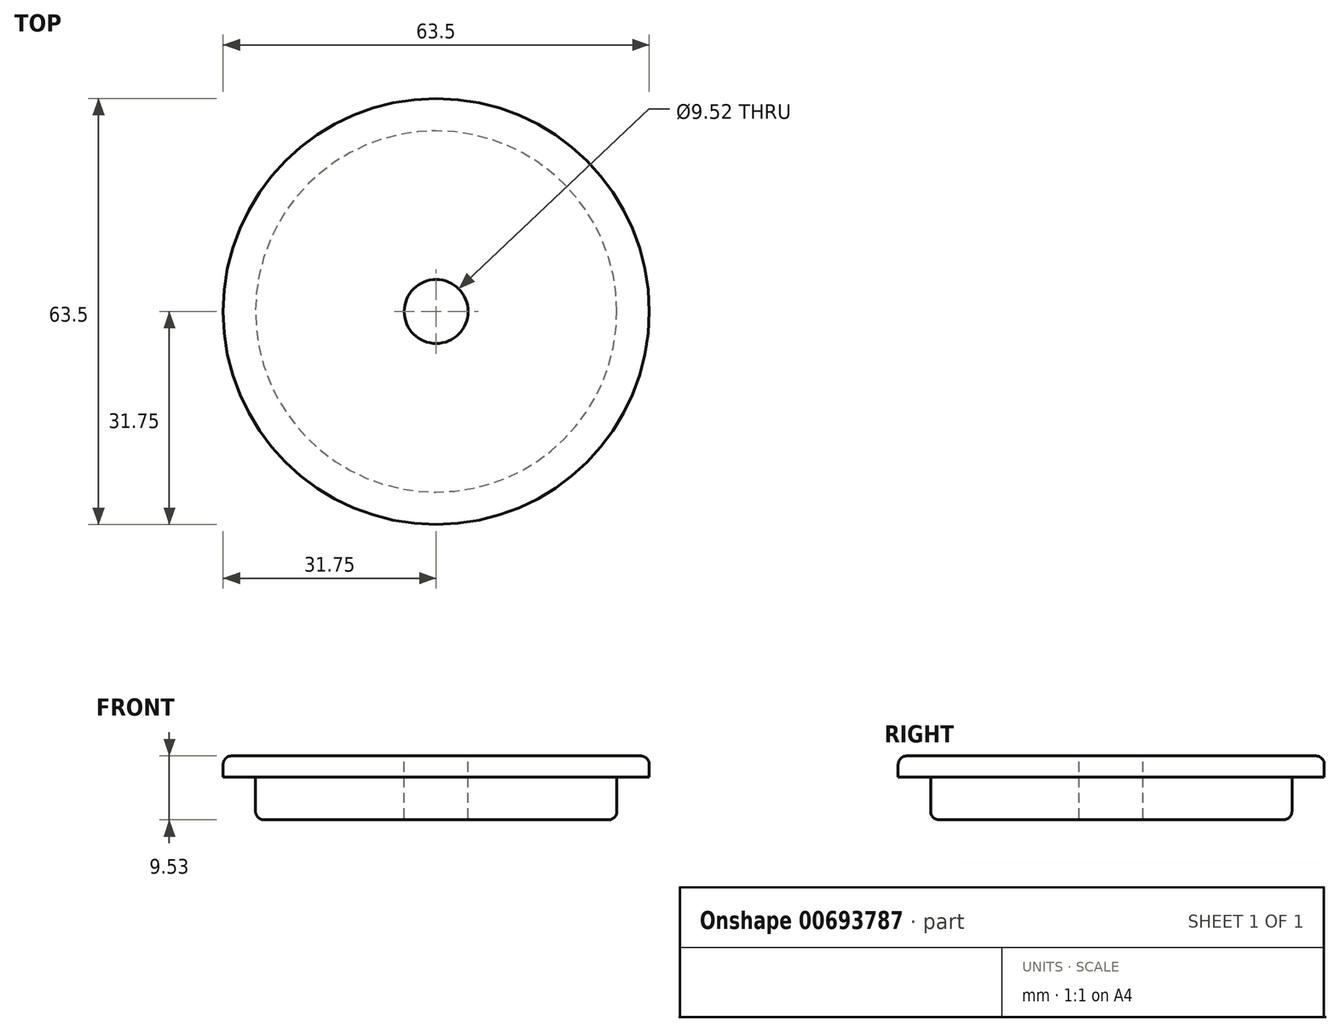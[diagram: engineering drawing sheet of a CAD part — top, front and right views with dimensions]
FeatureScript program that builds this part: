
annotation { "Feature Type Name" : "Feature", "Feature Type Description" : "" }
export const myFeature = defineFeature(function(context is Context, id is Id, definition is map)
    precondition{}
    {
        {
            var Q0;
            Q0=qCreatedBy(makeId("Top.planeOp"),FACE);
            var sketch = newSketch(context, id + "F0", { "sketchPlane" : qUnion([Q0])});
            skCircle(sketch, "E0", {"center": v(0, 0) * mm, "radius": 26.92 * mm});
            skSolve(sketch);
        }
        {
            var Q0;
            Q0=makeQuery(id+"F0.imprint","IMPRINT",FACE,{"disambiguationData":[TD([[makeQuery(id+"F0.imprint","IMPRINT",EDGE,{"derivedFrom":sQuery(id+"F0.wireOp",EDGE,"E0")}),1.0]])]});
            extrude(context, id + "F1", {"entities" : qUnion([Q0]), "flatOperationType" : FlatOperationType.REMOVE, "depth" : 6.35 * mm, "offsetDistance" : 25.4 * mm, "domain" : OperationDomain.MODEL});
        }
        {
            var Q0;
            Q0=makeQuery(id+"F1.opExtrude","CAP_FACE",FACE,{"disambiguationData":[OSD([sQuery(id+"F0.wireOp",EDGE,"E0")])],"isStart":false});
            var sketch = newSketch(context, id + "F2", { "sketchPlane" : qUnion([Q0])});
            skCircle(sketch, "E1", {"center": v(0, 0) * mm, "radius": 31.75 * mm});
            skSolve(sketch);
        }
        {
            var Q0;
            Q0=makeQuery(id+"F2.imprint","IMPRINT",FACE,{"disambiguationData":[TD([[makeQuery(id+"F2.imprint","IMPRINT",EDGE,{"derivedFrom":sQuery(id+"F2.wireOp",EDGE,"E1")}),1.0]])]});
            var Q1;
            Q1=makeQuery(id+"F2.imprint","IMPRINT",FACE,{"disambiguationData":[TD([[makeQuery(id+"F2.imprint","IMPRINT",EDGE,{"derivedFrom":makeQuery(id+"F1.opExtrude","CAP_EDGE",EDGE,{"disambiguationData":[OSD([sQuery(id+"F0.wireOp",EDGE,"E0")])],"isStart":false})}),1.0]])]});
            var Q2;
            Q2=sQuery(id+"F2.wireOp",EDGE,"E1");
            extrude(context, id + "F3", {"entities" : qUnion([Q0, Q1]), "operationType" : NewBodyOperationType.ADD, "surfaceEntities" : qUnion([Q2]), "depth" : 3.17 * mm, "offsetDistance" : 25.4 * mm});
        }
        {
            var Q0;
            Q0=makeQuery(id+"F3.opExtrude","CAP_FACE",FACE,{"disambiguationData":[OSD([sQuery(id+"F2.wireOp",EDGE,"E1")])],"isStart":false});
            var sketch = newSketch(context, id + "F4", { "sketchPlane" : qUnion([Q0])});
            skCircle(sketch, "E2", {"center": v(0, 0) * mm, "radius": 4.76 * mm});
            skSolve(sketch);
        }
        {
            var Q0;
            Q0=makeQuery(id+"F4.imprint","IMPRINT",FACE,{"disambiguationData":[TD([[makeQuery(id+"F4.imprint","IMPRINT",EDGE,{"derivedFrom":sQuery(id+"F4.wireOp",EDGE,"E2")}),1.0]])]});
            extrude(context, id + "F5", {"entities" : qUnion([Q0]), "operationType" : NewBodyOperationType.REMOVE, "oppositeDirection" : true, "depth" : 25.4 * mm, "offsetDistance" : 25.4 * mm});
        }
        {
            var Q0;
            Q0=makeQuery(id+"F3.opExtrude","CAP_EDGE",EDGE,{"disambiguationData":[OSD([sQuery(id+"F2.wireOp",EDGE,"E1")])],"isStart":false});
            fillet(context, id + "F6", {"entities" : qUnion([Q0]), "radius" : 1.27 * mm, "tangentPropagation" : true, "allowEdgeOverflow" : false});
        }
        {
            var Q0;
            Q0=makeQuery(id+"F1.opExtrude","CAP_EDGE",EDGE,{"disambiguationData":[OSD([sQuery(id+"F0.wireOp",EDGE,"E0")])],"isStart":true});
            fillet(context, id + "F7", {"entities" : qUnion([Q0]), "radius" : 1.27 * mm, "tangentPropagation" : true, "allowEdgeOverflow" : false});
        }
        {
            var Q0;
            Q0=makeQuery(id+"F5.boolean.opBoolean","COPY",EDGE,{"derivedFrom":makeQuery(id+"F5.opExtrude","CAP_EDGE",EDGE,{"disambiguationData":[OSD([sQuery(id+"F4.wireOp",EDGE,"E2")])],"isStart":true})});
            var Q1;
            Q1=makeQuery(id+"F5.boolean.opBoolean","INTERSECT",EDGE,{"derivedFrom":[makeQuery(id+"F1.opExtrude","CAP_FACE",FACE,{"disambiguationData":[OSD([sQuery(id+"F0.wireOp",EDGE,"E0")])],"isStart":true}),makeQuery(id+"F5.opExtrude","SWEPT_FACE",FACE,{"disambiguationData":[OSD([sQuery(id+"F4.wireOp",EDGE,"E2")])]})]});
            fillet(context, id + "F8", {"entities" : qUnion([Q0, Q1]), "radius" : 0.25 * mm, "tangentPropagation" : true, "allowEdgeOverflow" : false});
        }
    });
